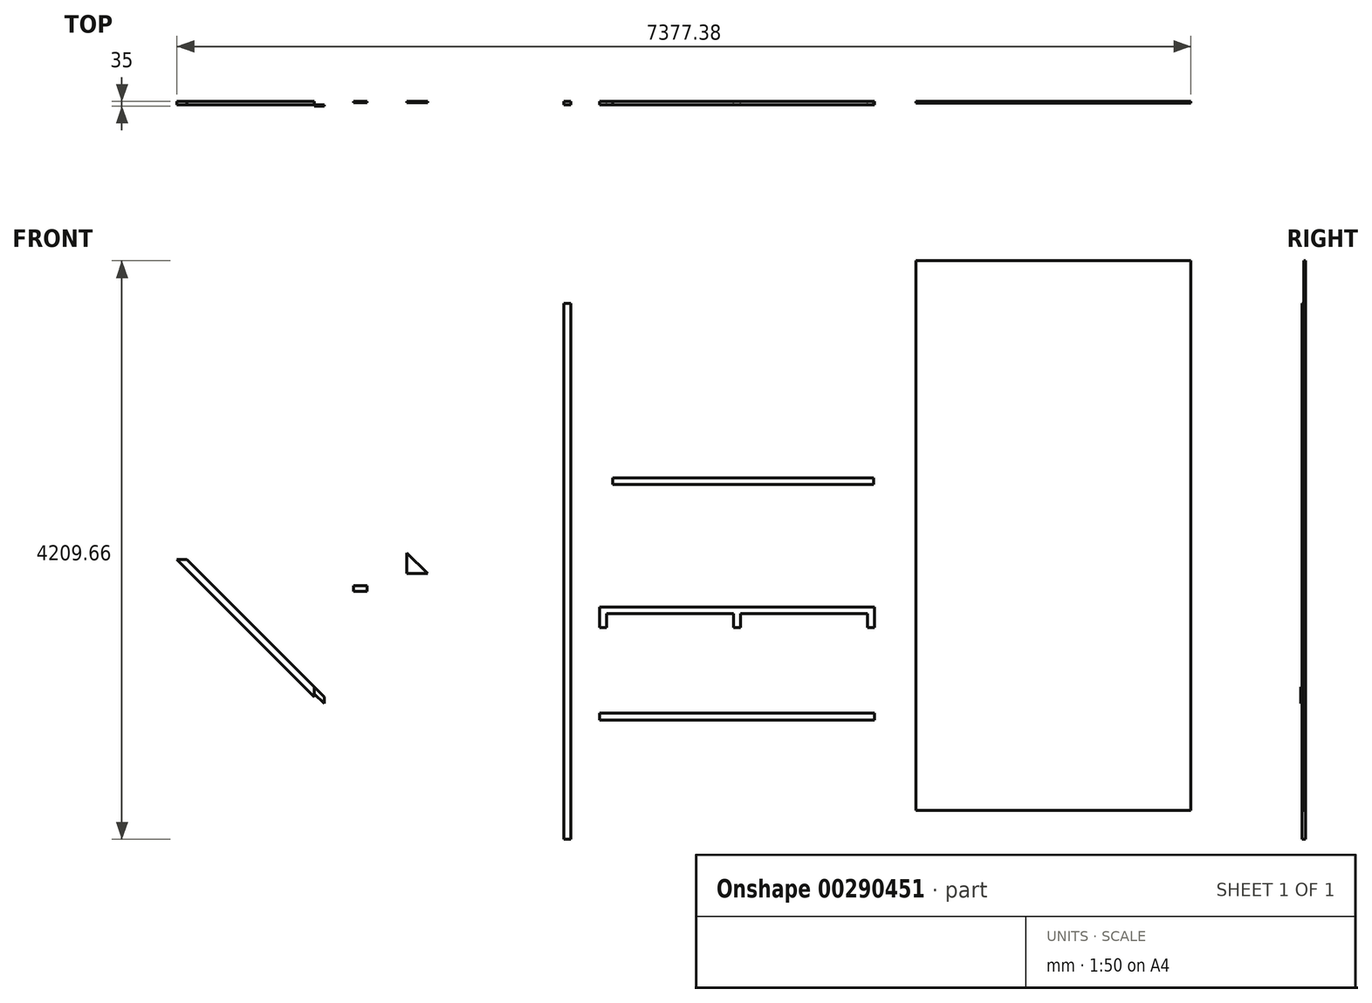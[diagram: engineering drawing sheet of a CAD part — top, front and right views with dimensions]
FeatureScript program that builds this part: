
annotation { "Feature Type Name" : "Feature", "Feature Type Description" : "" }
export const myFeature = defineFeature(function(context is Context, id is Id, definition is map)
    precondition{}
    {
        {
            var Q0;
            Q0=qCreatedBy(makeId("Front.planeOp"),FACE);
            var sketch = newSketch(context, id + "F0", { "sketchPlane" : qUnion([Q0])});
            skLineSegment(sketch, "E0.bottom", {"start": v(0, 0) * mm, "end": v(2000, 0) * mm});
            skLineSegment(sketch, "E0.top", {"start": v(0, -50) * mm, "end": v(2000, -50) * mm});
            skLineSegment(sketch, "E0.left", {"start": v(0, 0) * mm, "end": v(0, -50) * mm});
            skLineSegment(sketch, "E0.right", {"start": v(2000, 0) * mm, "end": v(2000, -50) * mm});
            skSolve(sketch);
        }
        {
            var Q0;
            Q0=makeQuery(id+"F0.imprint","IMPRINT",FACE,{"disambiguationData":[TD([[makeQuery(id+"F0.imprint","IMPRINT",EDGE,{"derivedFrom":sQuery(id+"F0.wireOp",EDGE,"E0.bottom")}),-1.0]])]});
            extrude(context, id + "F1", {"entities" : qUnion([Q0]), "depth" : 25 * mm});
        }
        {
            var Q0;
            Q0=qCreatedBy(makeId("Front.planeOp"),FACE);
            var sketch = newSketch(context, id + "F2", { "sketchPlane" : qUnion([Q0])});
            skLineSegment(sketch, "E1.bottom", {"start": v(-258.9, 2983.45) * mm, "end": v(-208.9, 2983.45) * mm});
            skLineSegment(sketch, "E1.top", {"start": v(-258.9, -916.55) * mm, "end": v(-208.9, -916.55) * mm});
            skLineSegment(sketch, "E1.left", {"start": v(-258.9, 2983.45) * mm, "end": v(-258.9, -916.55) * mm});
            skLineSegment(sketch, "E1.right", {"start": v(-208.9, 2983.45) * mm, "end": v(-208.9, -916.55) * mm});
            skSolve(sketch);
        }
        {
            var Q0;
            Q0 = qSketchRegion(id + "F2", true);
            extrude(context, id + "F3", {"entities" : qUnion([Q0]), "depth" : 25 * mm});
        }
        {
            var Q0;
            Q0=qCreatedBy(makeId("Front.planeOp"),FACE);
            var sketch = newSketch(context, id + "F4", { "sketchPlane" : qUnion([Q0])});
            skLineSegment(sketch, "E2.bottom", {"start": v(0, 774.03) * mm, "end": v(2000, 774.03) * mm});
            skLineSegment(sketch, "E3.top", {"start": v(0, 624.03) * mm, "end": v(50, 624.03) * mm});
            skLineSegment(sketch, "E3.right", {"start": v(50, 724.03) * mm, "end": v(50, 624.03) * mm});
            skLineSegment(sketch, "E4.top", {"start": v(2000, 624.03) * mm, "end": v(1950, 624.03) * mm});
            skLineSegment(sketch, "E4.right", {"start": v(1950, 724.03) * mm, "end": v(1950, 624.03) * mm});
            skPoint(sketch, "E5.endSnap0", {"position": v(1000, 630.93) * mm});
            skLineSegment(sketch, "E6.top", {"start": v(975, 624.03) * mm, "end": v(1025, 624.03) * mm});
            skLineSegment(sketch, "E6.left", {"start": v(975, 724.03) * mm, "end": v(975, 624.03) * mm});
            skLineSegment(sketch, "E6.right", {"start": v(1025, 724.03) * mm, "end": v(1025, 624.03) * mm});
            skLineSegment(sketch, "E7", {"start": v(1025, 724.03) * mm, "end": v(1950, 724.03) * mm});
            skLineSegment(sketch, "E8", {"start": v(975, 724.03) * mm, "end": v(50, 724.03) * mm});
            skLineSegment(sketch, "E9", {"start": v(0, 774.03) * mm, "end": v(0, 624.03) * mm});
            skLineSegment(sketch, "E10", {"start": v(2000, 774.03) * mm, "end": v(2000, 624.03) * mm});
            skSolve(sketch);
        }
        {
            var Q0;
            Q0 = qSketchRegion(id + "F4", true);
            extrude(context, id + "F5", {"entities" : qUnion([Q0]), "depth" : 25 * mm});
        }
        {
            var Q0;
            Q0=qCreatedBy(makeId("Front.planeOp"),FACE);
            var sketch = newSketch(context, id + "F6", { "sketchPlane" : qUnion([Q0])});
            skLineSegment(sketch, "E11.bottom", {"start": v(95.53, 1713.73) * mm, "end": v(1995.53, 1713.73) * mm});
            skLineSegment(sketch, "E11.top", {"start": v(95.53, 1663.73) * mm, "end": v(1995.53, 1663.73) * mm});
            skLineSegment(sketch, "E11.left", {"start": v(95.53, 1713.73) * mm, "end": v(95.53, 1663.73) * mm});
            skLineSegment(sketch, "E11.right", {"start": v(1995.53, 1713.73) * mm, "end": v(1995.53, 1663.73) * mm});
            skSolve(sketch);
        }
        {
            var Q0;
            Q0 = qSketchRegion(id + "F6", true);
            extrude(context, id + "F7", {"entities" : qUnion([Q0]), "depth" : 25 * mm});
        }
        {
            var Q0;
            Q0=qCreatedBy(makeId("Front.planeOp"),FACE);
            var sketch = newSketch(context, id + "F8", { "sketchPlane" : qUnion([Q0])});
            skLineSegment(sketch, "E12", {"start": v(-3075.03, 1120.32) * mm, "end": v(-2075.03, 120.32) * mm});
            skLineSegment(sketch, "E13", {"start": v(-3075.03, 1120.32) * mm, "end": v(-3004.32, 1120.32) * mm});
            skLineSegment(sketch, "E14", {"start": v(-2075.03, 191.03) * mm, "end": v(-2075.03, 120.32) * mm});
            skLineSegment(sketch, "E15", {"start": v(-2075.03, 191.03) * mm, "end": v(-3004.32, 1120.32) * mm});
            skSolve(sketch);
        }
        {
            var Q0;
            Q0 = qSketchRegion(id + "F8", true);
            extrude(context, id + "F9", {"entities" : qUnion([Q0]), "depth" : 25 * mm});
        }
        {
            var Q0;
            Q0=makeQuery(id+"F9.opExtrude","CAP_FACE",FACE,{"disambiguationData":[OSD([sQuery(id+"F8.wireOp",EDGE,"E12"),sQuery(id+"F8.wireOp",EDGE,"E13"),sQuery(id+"F8.wireOp",EDGE,"E14"),sQuery(id+"F8.wireOp",EDGE,"E15")])],"isStart":false});
            var sketch = newSketch(context, id + "F10", { "sketchPlane" : qUnion([Q0])});
            skLineSegment(sketch, "E16", {"start": v(-2075.03, 191.03) * mm, "end": v(-2004.32, 120.32) * mm});
            skLineSegment(sketch, "E17", {"start": v(-2004.32, 120.32) * mm, "end": v(-2004.32, 70.32) * mm});
            skLineSegment(sketch, "E18", {"start": v(-2004.32, 70.32) * mm, "end": v(-2075.03, 141.03) * mm});
            skLineSegment(sketch, "E19", {"start": v(-2075.03, 141.03) * mm, "end": v(-2075.03, 191.03) * mm});
            skSolve(sketch);
        }
        {
            var Q0;
            Q0=makeQuery(id+"F10.imprint","IMPRINT",FACE,{"disambiguationData":[TD([[makeQuery(id+"F10.imprint","IMPRINT",EDGE,{"derivedFrom":sQuery(id+"F10.wireOp",EDGE,"E16")}),-1.0]])]});
            extrude(context, id + "F11", {"entities" : qUnion([Q0]), "depth" : 10 * mm});
        }
        {
            var Q0;
            Q0=qCreatedBy(makeId("Front.planeOp"),FACE);
            var sketch = newSketch(context, id + "F12", { "sketchPlane" : qUnion([Q0])});
            skLineSegment(sketch, "E20.bottom", {"start": v(-1791.71, 928.23) * mm, "end": v(-1691.71, 928.23) * mm});
            skLineSegment(sketch, "E20.top", {"start": v(-1791.71, 888.23) * mm, "end": v(-1691.71, 888.23) * mm});
            skLineSegment(sketch, "E20.left", {"start": v(-1791.71, 928.23) * mm, "end": v(-1791.71, 888.23) * mm});
            skLineSegment(sketch, "E20.right", {"start": v(-1691.71, 928.23) * mm, "end": v(-1691.71, 888.23) * mm});
            skSolve(sketch);
        }
        {
            var Q0;
            Q0 = qSketchRegion(id + "F12", true);
            extrude(context, id + "F13", {"entities" : qUnion([Q0]), "depth" : 10 * mm});
        }
        {
            var Q0;
            Q0=qCreatedBy(makeId("Front.planeOp"),FACE);
            var sketch = newSketch(context, id + "F14", { "sketchPlane" : qUnion([Q0])});
            skLineSegment(sketch, "E21", {"start": v(-1401.66, 1167.6) * mm, "end": v(-1401.66, 1017.6) * mm});
            skLineSegment(sketch, "E22", {"start": v(-1401.66, 1017.6) * mm, "end": v(-1251.66, 1017.6) * mm});
            skLineSegment(sketch, "E23", {"start": v(-1251.66, 1017.6) * mm, "end": v(-1401.66, 1167.6) * mm});
            skSolve(sketch);
        }
        {
            var Q0;
            Q0 = qSketchRegion(id + "F14", true);
            extrude(context, id + "F15", {"entities" : qUnion([Q0]), "depth" : 10 * mm});
        }
        {
            var Q0;
            Q0=qCreatedBy(makeId("Front.planeOp"),FACE);
            var sketch = newSketch(context, id + "F16", { "sketchPlane" : qUnion([Q0])});
            skLineSegment(sketch, "E24.bottom", {"start": v(2302.35, 3293.1) * mm, "end": v(4302.35, 3293.1) * mm});
            skLineSegment(sketch, "E24.top", {"start": v(2302.35, -706.9) * mm, "end": v(4302.35, -706.9) * mm});
            skLineSegment(sketch, "E24.left", {"start": v(2302.35, 3293.1) * mm, "end": v(2302.35, -706.9) * mm});
            skLineSegment(sketch, "E24.right", {"start": v(4302.35, 3293.1) * mm, "end": v(4302.35, -706.9) * mm});
            skSolve(sketch);
        }
        {
            var Q0;
            Q0=makeQuery(id+"F16.imprint","IMPRINT",FACE,{"disambiguationData":[TD([[makeQuery(id+"F16.imprint","IMPRINT",EDGE,{"derivedFrom":sQuery(id+"F16.wireOp",EDGE,"E24.bottom")}),-1.0]])]});
            extrude(context, id + "F17", {"entities" : qUnion([Q0]), "depth" : 12 * mm});
        }
    });
